# Revit family: Sink-Wall_Mount-Lavatory-KOHLER-Modern_Life-GB112K_1
name_source: partatom
category: Plumbing Fixtures
revit_build: Autodesk Revit 2017 (Build: 20160225_1515(x64)
units: mm (PartAtom-declared; Revit-internal decimal feet)

## family parameters
Cut with Voids When Loaded = No
Host = Face
OmniClass Number = 23.31.13.00
OmniClass Title = Sinks
Part Type = Normal
Room Calculation Point = No
Round Connector Dimension = Use Diameter
Shared = No

## types (2) — shared parameters
ADA Compliant = No
Assembly Code = D2010400
CW Connection = No
Cold Water Inlet = Cold Water Inlet
Date Modified = 09/29/2021
Default Elevation = 36"
Drain Included = No
Finish = Kohler-Vitreous_China-0-White
HW Connection = No
Height = 5"
Hot Water Inlet = Hot Water Inlet
Length = 9 13/16"
Manufacturer = KOHLER Co.
Master Format 2014 = 22 41 16
Master Format 2014 Name = Residential Lavatories and Sinks
Material = Vitreous China
Product Name = ModernLife
URL = https://www.kohler.co.uk
Vent Connection = No
Waste Connection = Yes
Waste Water Outlet = Waste Water Outlet
WaterSense Certified = No
Width = 19 5/8"

## per-type parameters (varying)
| type | Description | Left Side Faucet Hole | Model | Right Side Faucet Hole | Type |
| Left Side Faucet Hole, 00-White | Handwash basin with glazed underside - left hand tap deck | Yes | GB112K-55-00 | No | 1 |
| Right Side Faucet Hole, 00-White | Handwash basin with glazed underside - right hand tap deck | No | GB112K-56-00 | Yes | 2 |

## geometry (parser evidence)
native form markers: Sweep x5
no freeform markers — native parametric forms only
